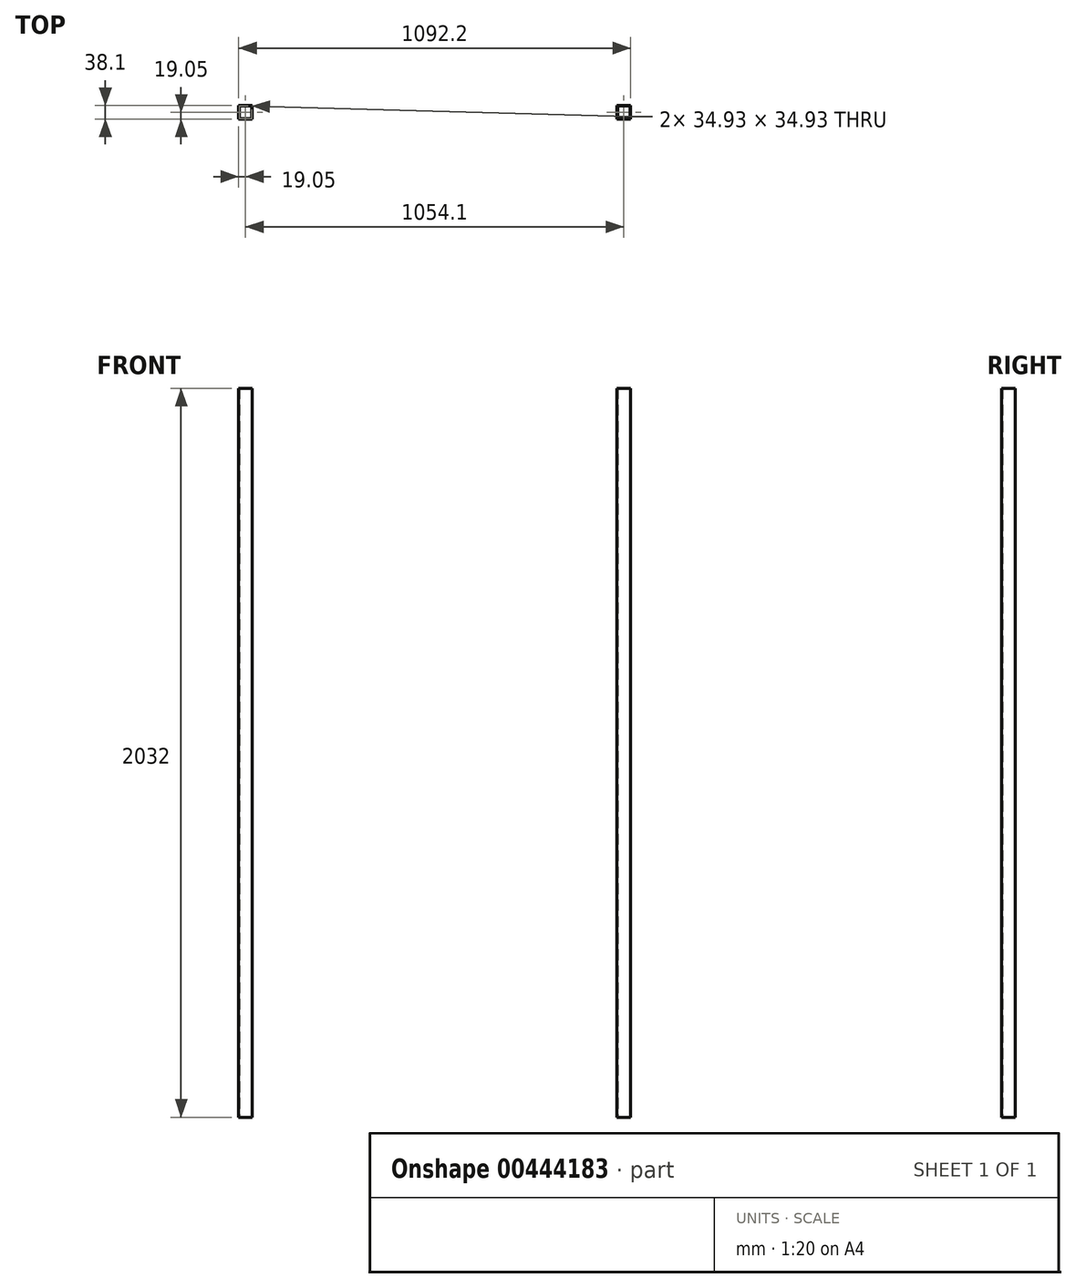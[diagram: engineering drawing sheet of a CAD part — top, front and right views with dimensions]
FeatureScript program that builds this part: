
annotation { "Feature Type Name" : "Feature", "Feature Type Description" : "" }
export const myFeature = defineFeature(function(context is Context, id is Id, definition is map)
    precondition{}
    {
        {
            var Q0;
            Q0=qCreatedBy(makeId("Front.planeOp"),FACE);
            var sketch = newSketch(context, id + "F0", { "sketchPlane" : qUnion([Q0])});
            skLineSegment(sketch, "E0.bottom", {"start": v(0, 0) * mm, "end": v(1016, 0) * mm});
            skLineSegment(sketch, "E0.top", {"start": v(0, 2032) * mm, "end": v(1016, 2032) * mm});
            skLineSegment(sketch, "E0.left", {"start": v(0, 0) * mm, "end": v(0, 2032) * mm});
            skLineSegment(sketch, "E0.right", {"start": v(1016, 0) * mm, "end": v(1016, 2032) * mm});
            skSolve(sketch);
        }
        {
            var Q0;
            Q0=qCreatedBy(makeId("Top.planeOp"),FACE);
            var sketch = newSketch(context, id + "F1", { "sketchPlane" : qUnion([Q0])});
            skLineSegment(sketch, "E1.bottom", {"start": v(0, 0) * mm, "end": v(-38.1, 0) * mm});
            skLineSegment(sketch, "E1.top", {"start": v(0, -38.1) * mm, "end": v(-38.1, -38.1) * mm});
            skLineSegment(sketch, "E1.left", {"start": v(0, 0) * mm, "end": v(0, -38.1) * mm});
            skLineSegment(sketch, "E1.right", {"start": v(-38.1, 0) * mm, "end": v(-38.1, -38.1) * mm});
            skLineSegment(sketch, "E2.bottom", {"start": v(1016, 0) * mm, "end": v(1054.1, 0) * mm});
            skLineSegment(sketch, "E2.top", {"start": v(1016, -38.1) * mm, "end": v(1054.1, -38.1) * mm});
            skLineSegment(sketch, "E2.left", {"start": v(1016, 0) * mm, "end": v(1016, -38.1) * mm});
            skLineSegment(sketch, "E2.right", {"start": v(1054.1, 0) * mm, "end": v(1054.1, -38.1) * mm});
            skLineSegment(sketch, "E3.0", {"start": v(-1.59, -1.59) * mm, "end": v(-36.51, -1.59) * mm});
            skLineSegment(sketch, "E3.1", {"start": v(-1.59, -1.59) * mm, "end": v(-1.59, -36.51) * mm});
            skLineSegment(sketch, "E3.2", {"start": v(-1.59, -36.51) * mm, "end": v(-36.51, -36.51) * mm});
            skLineSegment(sketch, "E3.3", {"start": v(-36.51, -1.59) * mm, "end": v(-36.51, -36.51) * mm});
            skLineSegment(sketch, "E4.0", {"start": v(1052.51, -1.59) * mm, "end": v(1052.51, -36.51) * mm});
            skLineSegment(sketch, "E4.1", {"start": v(1017.59, -1.59) * mm, "end": v(1052.51, -1.59) * mm});
            skLineSegment(sketch, "E4.2", {"start": v(1017.59, -1.59) * mm, "end": v(1017.59, -36.51) * mm});
            skLineSegment(sketch, "E4.3", {"start": v(1017.59, -36.51) * mm, "end": v(1052.51, -36.51) * mm});
            skSolve(sketch);
        }
        {
            var Q0;
            Q0 = qSketchRegion(id + "F1", true);
            var Q1;
            Q1=sQuery(id+"F0.wireOp",VERTEX,"E0.left.end");
            extrude(context, id + "F2", {"entities" : qUnion([Q0]), "endBound" : BoundingType.UP_TO_VERTEX, "endBoundEntityVertex" : qUnion([Q1]), "depth" : 25.4 * mm});
        }
    });
